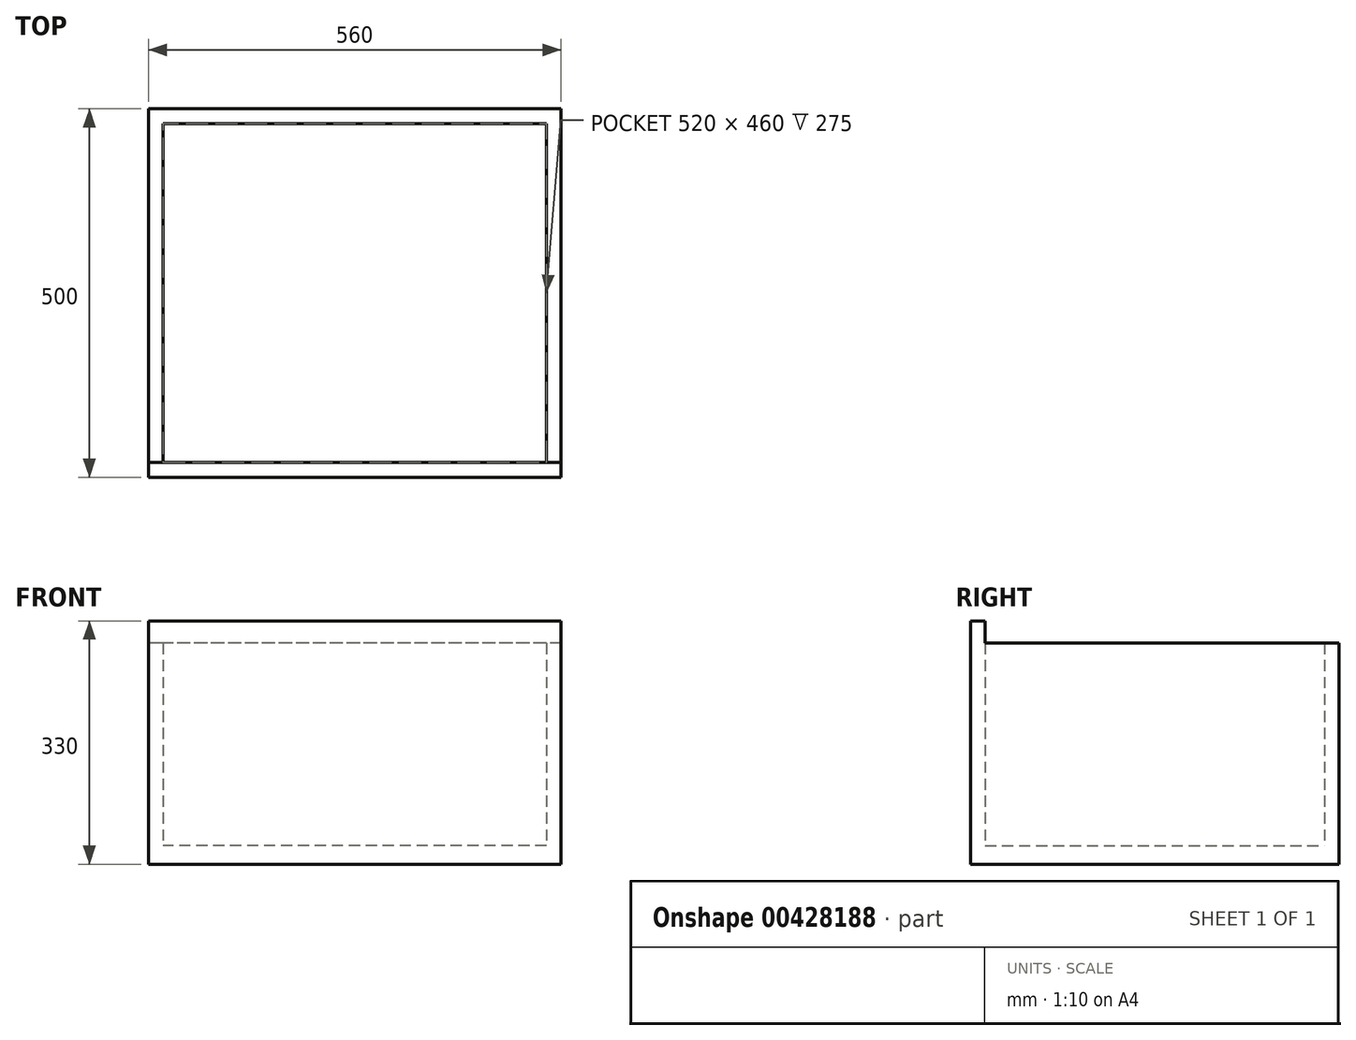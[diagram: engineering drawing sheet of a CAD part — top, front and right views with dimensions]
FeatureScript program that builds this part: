
annotation { "Feature Type Name" : "Feature", "Feature Type Description" : "" }
export const myFeature = defineFeature(function(context is Context, id is Id, definition is map)
    precondition{}
    {
        {
            var Q0;
            Q0=qCreatedBy(makeId("Top.planeOp"),FACE);
            var sketch = newSketch(context, id + "F0", { "sketchPlane" : qUnion([Q0])});
            skLineSegment(sketch, "E0.bottom", {"start": v(280, -250) * mm, "end": v(-280, -250) * mm});
            skLineSegment(sketch, "E0.top", {"start": v(280, 250) * mm, "end": v(-280, 250) * mm});
            skLineSegment(sketch, "E0.left", {"start": v(280, -250) * mm, "end": v(280, 250) * mm});
            skLineSegment(sketch, "E0.right", {"start": v(-280, -250) * mm, "end": v(-280, 250) * mm});
            skPoint(sketch, "E0.middle", {"position": v(0, 0) * mm});
            skLineSegment(sketch, "E1.0", {"start": v(-260, -250) * mm, "end": v(-260, 250) * mm});
            skLineSegment(sketch, "E2.0", {"start": v(280, 230) * mm, "end": v(-280, 230) * mm});
            skLineSegment(sketch, "E3.0", {"start": v(260, -250) * mm, "end": v(260, 250) * mm});
            skLineSegment(sketch, "E4.0", {"start": v(280, -230) * mm, "end": v(-280, -230) * mm});
            skSolve(sketch);
        }
        {
            var Q0;
            {var subQ0=sQuery(id+"F0.wireOp",EDGE,"E2.0");var subQ1=sQuery(id+"F0.wireOp",EDGE,"E0.right");var subQ2=makeQuery(id+"F0.imprint","INTERSECT",VERTEX,{"derivedFrom":[subQ1,subQ0]});Q0=makeQuery(id+"F0.imprint","IMPRINT",FACE,{"disambiguationData":[TD([[makeQuery(id+"F0.imprint","IMPRINT",EDGE,{"disambiguationData":[TD([[subQ2,1.0]])],"derivedFrom":subQ1}),-1.0]])]});}
            var Q1;
            {var subQ0=sQuery(id+"F0.wireOp",EDGE,"E0.right");var subQ1=sQuery(id+"F0.wireOp",EDGE,"E0.top");var subQ2=makeQuery(id+"F0.imprint","INTERSECT",VERTEX,{"derivedFrom":[subQ1,subQ0]});Q1=makeQuery(id+"F0.imprint","IMPRINT",FACE,{"disambiguationData":[TD([[makeQuery(id+"F0.imprint","IMPRINT",EDGE,{"disambiguationData":[TD([[subQ2,1.0]])],"derivedFrom":subQ1}),1.0]])]});}
            var Q2;
            {var subQ0=sQuery(id+"F0.wireOp",EDGE,"E1.0");var subQ1=sQuery(id+"F0.wireOp",EDGE,"E0.top");var subQ2=makeQuery(id+"F0.imprint","INTERSECT",VERTEX,{"derivedFrom":[subQ1,subQ0]});Q2=makeQuery(id+"F0.imprint","IMPRINT",FACE,{"disambiguationData":[TD([[makeQuery(id+"F0.imprint","IMPRINT",EDGE,{"disambiguationData":[TD([[subQ2,1.0]])],"derivedFrom":subQ1}),1.0]])]});}
            var Q3;
            {var subQ0=sQuery(id+"F0.wireOp",EDGE,"E0.left");var subQ1=sQuery(id+"F0.wireOp",EDGE,"E0.top");var subQ2=makeQuery(id+"F0.imprint","INTERSECT",VERTEX,{"derivedFrom":[subQ1,subQ0]});Q3=makeQuery(id+"F0.imprint","IMPRINT",FACE,{"disambiguationData":[TD([[makeQuery(id+"F0.imprint","IMPRINT",EDGE,{"disambiguationData":[TD([[subQ2,-1.0]])],"derivedFrom":subQ1}),1.0]])]});}
            var Q4;
            {var subQ0=sQuery(id+"F0.wireOp",EDGE,"E2.0");var subQ1=sQuery(id+"F0.wireOp",EDGE,"E0.left");var subQ2=makeQuery(id+"F0.imprint","INTERSECT",VERTEX,{"derivedFrom":[subQ1,subQ0]});Q4=makeQuery(id+"F0.imprint","IMPRINT",FACE,{"disambiguationData":[TD([[makeQuery(id+"F0.imprint","IMPRINT",EDGE,{"disambiguationData":[TD([[subQ2,1.0]])],"derivedFrom":subQ1}),1.0]])]});}
            extrude(context, id + "F1", {"entities" : qUnion([Q0, Q1, Q2, Q3, Q4]), "depth" : 300 * mm});
        }
        {
            var Q0;
            {var subQ0=sQuery(id+"F0.wireOp",EDGE,"E0.left");var subQ1=sQuery(id+"F0.wireOp",EDGE,"E0.bottom");var subQ2=makeQuery(id+"F0.imprint","INTERSECT",VERTEX,{"derivedFrom":[subQ1,subQ0]});Q0=makeQuery(id+"F0.imprint","IMPRINT",FACE,{"disambiguationData":[TD([[makeQuery(id+"F0.imprint","IMPRINT",EDGE,{"disambiguationData":[TD([[subQ2,-1.0]])],"derivedFrom":subQ1}),-1.0]])]});}
            var Q1;
            {var subQ0=sQuery(id+"F0.wireOp",EDGE,"E1.0");var subQ1=sQuery(id+"F0.wireOp",EDGE,"E0.bottom");var subQ2=makeQuery(id+"F0.imprint","INTERSECT",VERTEX,{"derivedFrom":[subQ1,subQ0]});Q1=makeQuery(id+"F0.imprint","IMPRINT",FACE,{"disambiguationData":[TD([[makeQuery(id+"F0.imprint","IMPRINT",EDGE,{"disambiguationData":[TD([[subQ2,1.0]])],"derivedFrom":subQ1}),-1.0]])]});}
            var Q2;
            {var subQ0=sQuery(id+"F0.wireOp",EDGE,"E0.right");var subQ1=sQuery(id+"F0.wireOp",EDGE,"E0.bottom");var subQ2=makeQuery(id+"F0.imprint","INTERSECT",VERTEX,{"derivedFrom":[subQ1,subQ0]});Q2=makeQuery(id+"F0.imprint","IMPRINT",FACE,{"disambiguationData":[TD([[makeQuery(id+"F0.imprint","IMPRINT",EDGE,{"disambiguationData":[TD([[subQ2,1.0]])],"derivedFrom":subQ1}),-1.0]])]});}
            extrude(context, id + "F2", {"entities" : qUnion([Q0, Q1, Q2]), "operationType" : NewBodyOperationType.ADD, "depth" : 330 * mm});
        }
        {
            var Q0;
            {var subQ0=sQuery(id+"F0.wireOp",EDGE,"E4.0");var subQ1=sQuery(id+"F0.wireOp",EDGE,"E1.0");var subQ2=makeQuery(id+"F0.imprint","INTERSECT",VERTEX,{"derivedFrom":[subQ1,subQ0]});Q0=makeQuery(id+"F0.imprint","IMPRINT",FACE,{"disambiguationData":[TD([[makeQuery(id+"F0.imprint","IMPRINT",EDGE,{"disambiguationData":[TD([[subQ2,-1.0]])],"derivedFrom":subQ1}),-1.0]])]});}
            extrude(context, id + "F3", {"entities" : qUnion([Q0]), "operationType" : NewBodyOperationType.ADD, "depth" : 25 * mm});
        }
    });
